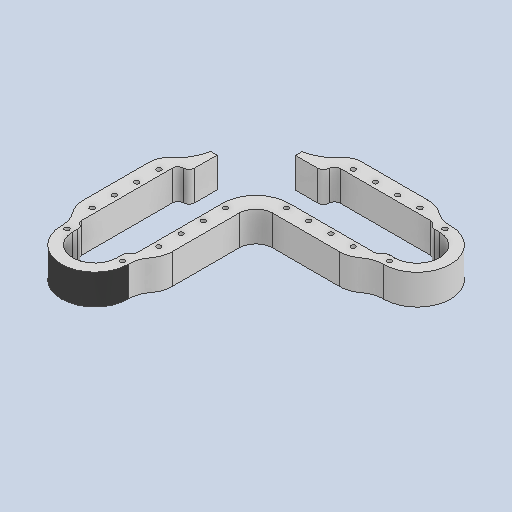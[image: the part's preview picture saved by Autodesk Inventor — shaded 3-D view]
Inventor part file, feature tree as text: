
AUTODESK INVENTOR PART (.ipt)
format: ipt  version: 2025.1 (Build 291241020, 241B)  size: 280,576 bytes
history: native  units: in
note: dims shown in document units (in); Inventor stores cm internally (conversion verified against a paired STEP export)
features: plane x1, extrude x1, sketch x1
ambient origin geometry x8: Origin, YZ Plane, XZ Plane, XY Plane, X Axis, Y Axis, Z Axis, Center Point
bodies: Solid1 (feature_tree)
feature tree (3):
  plane  "Work Plane1"
  extrude  "Extrusion2"  Depth=0.25in
  sketch  "Sketch2"  dims[d55=1.355in d56=0.0in d62=0.2087in d64=0.2832in d65=1.0084in d72=0.5in d73=0.75in d74=0.75in d75=0.2528in d76=1.0in d77=1.0in d78=1.0in d104=0.25in d105=0.25in d106=0.25in d107=0.25in d109=0.25in d110=0.25in d111=0.75in d112=0.75in d114=1.375in d115=1.25in d116=1.0in d117=1.0in d118=1.0in d122=1.5in d124=0.2087in d125=0.25in d126=0.25in d127=0.25in d128=0.2357in d129=0.5in d130=0.75in d131=0.75in d132=0.6687in d133=0.25in d134=3.817in d135=0.2165in d136=1.0in d137=4.0379in d138=11.282in d139=1.0in d140=0.2357in d141=0.5in d142=0.5in d143=0.75in d144=0.75in d145=0.5in d146=1.0in d147=0.75in d148=1.0in d149=1.0in d150=1.0in d151=0.2087in d152=0.75in d153=0.4999in d154=0.75in d155=1.5043in d156=1.0042in d157=0.25in d158=0.25in d159=3.8254in d160=0.433in d161=0.2165in d162=0.2357in d163=0.2087in d164=1.5048in d165=0.2357in d166=0.25in d167=0.25in d168=0.433in d169=0.2087in d170=0.2087in d171=1.8433in d172=1.0084in d173=2.0in d174=0.75in d175=0.5769in d176=2.9857in d177=0.2087in d178=0.2087in d179=0.433in d180=0.2165in d181=0.125in d182=2.9857in d183=4.067in d184=0.2832in d185=1.0084in d186=2.0in d187=0.75in d188=0.25in d189=1.1798in d190=0.5655in d191=0.1898in]
